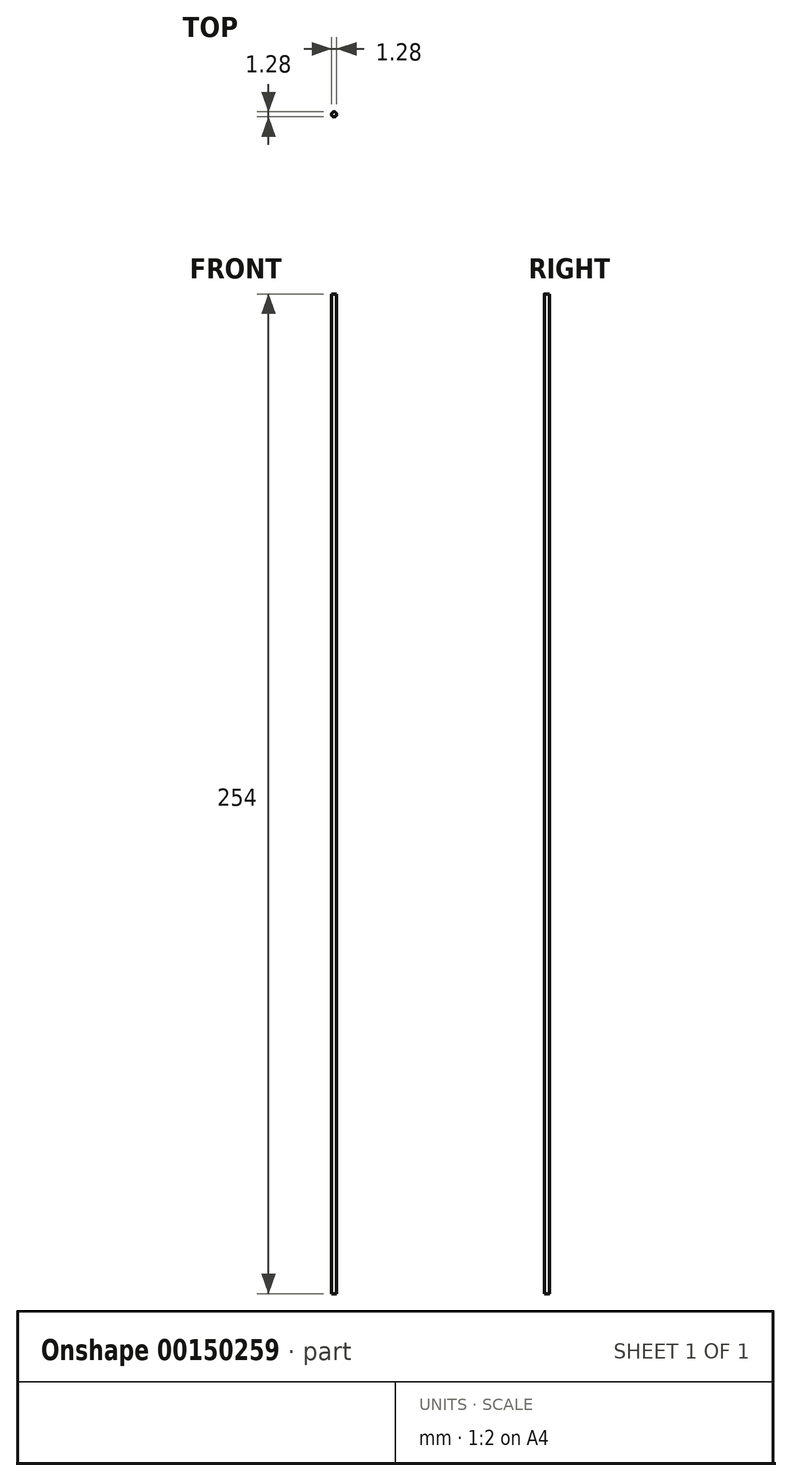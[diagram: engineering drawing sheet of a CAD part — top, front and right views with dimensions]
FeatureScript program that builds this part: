
annotation { "Feature Type Name" : "Feature", "Feature Type Description" : "" }
export const myFeature = defineFeature(function(context is Context, id is Id, definition is map)
    precondition{}
    {
        {
            var Q0;
            Q0=qCreatedBy(makeId("Top.planeOp"),FACE);
            var sketch = newSketch(context, id + "F0", { "sketchPlane" : qUnion([Q0])});
            skCircle(sketch, "E0", {"center": v(0, 0) * mm, "radius": 0.64 * mm});
            skSolve(sketch);
        }
        {
            var Q0;
            Q0=qSketchRegion(id+"F0",true);
            extrude(context, id + "F1", {"entities" : qUnion([Q0]), "depth" : 254 * mm});
        }
    });
